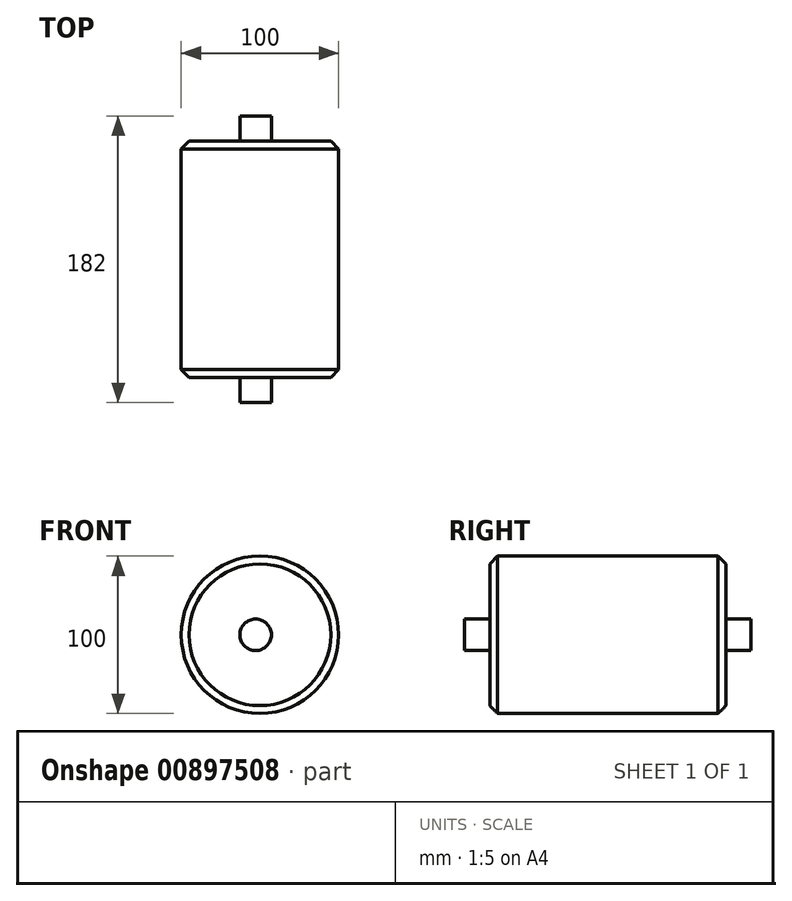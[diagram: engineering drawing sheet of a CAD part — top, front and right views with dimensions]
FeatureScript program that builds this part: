
annotation { "Feature Type Name" : "Feature", "Feature Type Description" : "" }
export const myFeature = defineFeature(function(context is Context, id is Id, definition is map)
    precondition{}
    {
        {
            var Q0;
            Q0=qCreatedBy(makeId("Front.planeOp"),FACE);
            var sketch = newSketch(context, id + "F0", { "sketchPlane" : qUnion([Q0])});
            skCircle(sketch, "E0", {"center": v(2.73, 0) * mm, "radius": 50 * mm});
            skSolve(sketch);
        }
        {
            var Q0;
            Q0=makeQuery(id+"F0.imprint","IMPRINT",FACE,{"disambiguationData":[TD([[makeQuery(id+"F0.imprint","IMPRINT",EDGE,{"derivedFrom":sQuery(id+"F0.wireOp",EDGE,"E0")}),1.0]])]});
            extrude(context, id + "F1", {"entities" : qUnion([Q0]), "depth" : 150 * mm, "offsetDistance" : 25.4 * mm});
        }
        {
            var Q0;
            Q0=makeQuery(id+"F1.opExtrude","CAP_FACE",FACE,{"disambiguationData":[OSD([sQuery(id+"F0.wireOp",EDGE,"E0")])],"isStart":false});
            chamfer(context, id + "F2", {"entities" : qUnion([Q0]), "width" : 5 * mm, "tangentPropagation" : true});
        }
        {
            var Q0;
            Q0=makeQuery(id+"F1.opExtrude","CAP_FACE",FACE,{"disambiguationData":[OSD([sQuery(id+"F0.wireOp",EDGE,"E0")])],"isStart":true});
            chamfer(context, id + "F3", {"entities" : qUnion([Q0]), "width" : 5 * mm, "tangentPropagation" : true});
        }
        {
            var Q0;
            Q0=makeQuery(id+"F1.opExtrude","CAP_FACE",FACE,{"disambiguationData":[OSD([sQuery(id+"F0.wireOp",EDGE,"E0")])],"isStart":false});
            var sketch = newSketch(context, id + "F4", { "sketchPlane" : qUnion([Q0])});
            skCircle(sketch, "E1", {"center": v(0, 0) * mm, "radius": 10 * mm});
            skSolve(sketch);
        }
        {
            var Q0;
            Q0=makeQuery(id+"F4.imprint","IMPRINT",FACE,{"disambiguationData":[TD([[makeQuery(id+"F4.imprint","IMPRINT",EDGE,{"derivedFrom":sQuery(id+"F4.wireOp",EDGE,"E1")}),1.0]])]});
            extrude(context, id + "F5", {"entities" : qUnion([Q0]), "operationType" : NewBodyOperationType.ADD, "depth" : 16 * mm, "offsetDistance" : 25.4 * mm});
        }
        {
            var Q0;
            Q0=makeQuery(id+"F1.opExtrude","CAP_FACE",FACE,{"disambiguationData":[OSD([sQuery(id+"F0.wireOp",EDGE,"E0")])],"isStart":true});
            var sketch = newSketch(context, id + "F6", { "sketchPlane" : qUnion([Q0])});
            skCircle(sketch, "E2", {"center": v(0, 0) * mm, "radius": 10 * mm});
            skSolve(sketch);
        }
        {
            var Q0;
            Q0=makeQuery(id+"F6.imprint","IMPRINT",FACE,{"disambiguationData":[TD([[makeQuery(id+"F6.imprint","IMPRINT",EDGE,{"derivedFrom":sQuery(id+"F6.wireOp",EDGE,"E2")}),1.0]])]});
            extrude(context, id + "F7", {"entities" : qUnion([Q0]), "operationType" : NewBodyOperationType.ADD, "depth" : 16 * mm, "offsetDistance" : 25.4 * mm});
        }
    });
